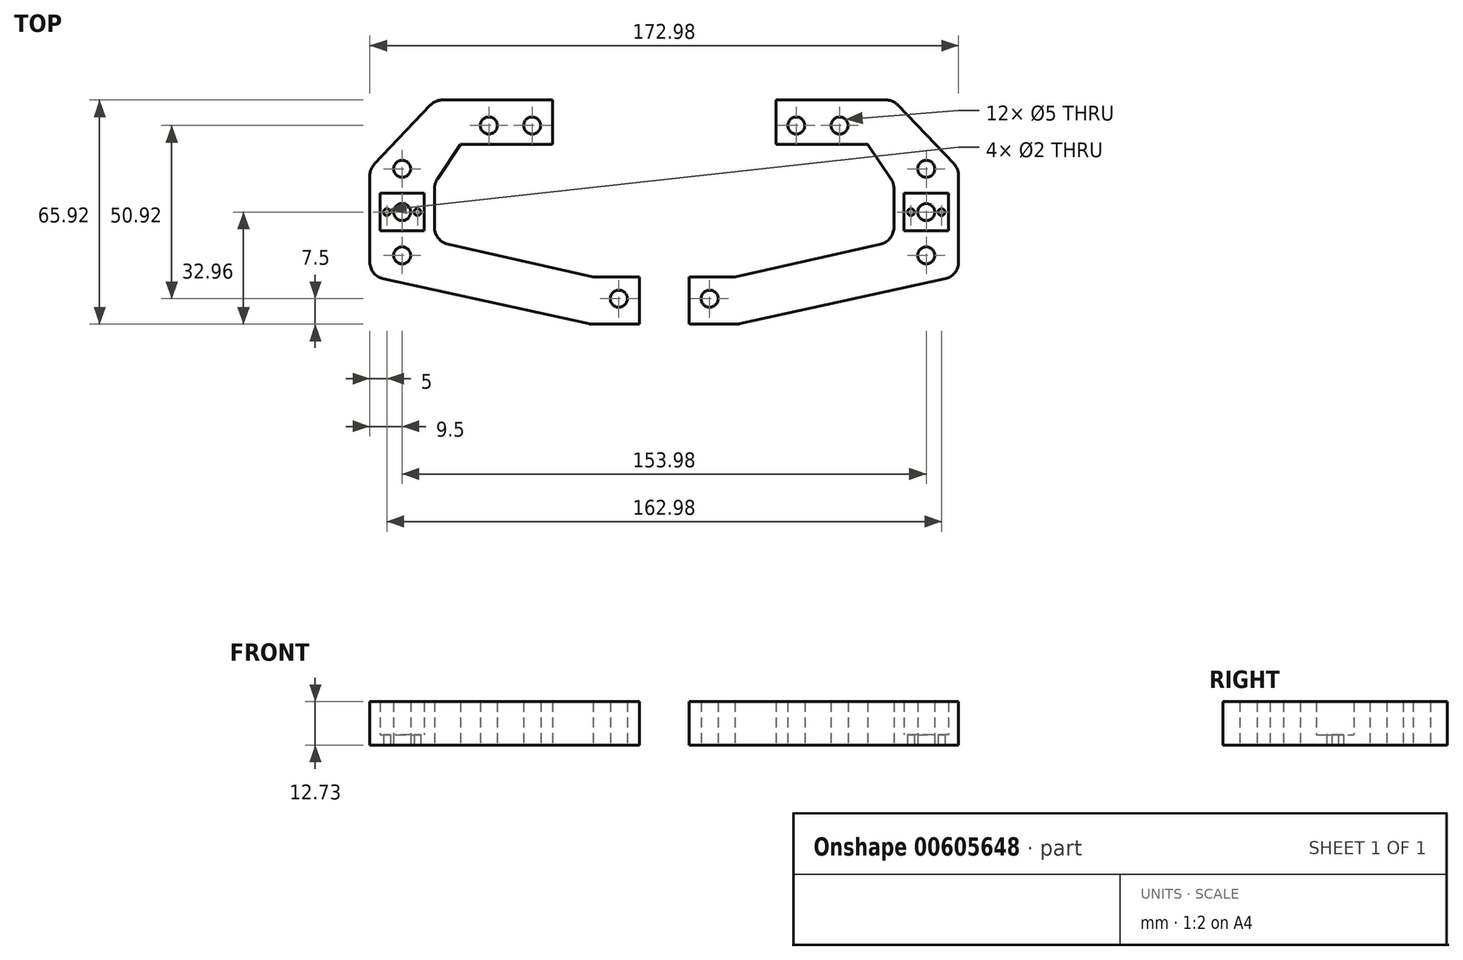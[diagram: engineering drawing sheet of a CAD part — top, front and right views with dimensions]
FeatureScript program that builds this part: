
annotation { "Feature Type Name" : "Feature", "Feature Type Description" : "" }
export const myFeature = defineFeature(function(context is Context, id is Id, definition is map)
    precondition{}
    {
        {
            var Q0;
            Q0=qCreatedBy(makeId("Top.planeOp"),FACE);
            var sketch = newSketch(context, id + "F0", { "sketchPlane" : qUnion([Q0])});
            skPoint(sketch, "E0", {"position": v(0, 0) * mm});
            skPoint(sketch, "E1", {"position": v(0, -50.92) * mm});
            skPoint(sketch, "E2", {"position": v(25.46, -50.92) * mm});
            skPoint(sketch, "E3", {"position": v(-12.73, 0) * mm});
            skPoint(sketch, "E4", {"position": v(0, -25.46) * mm});
            skPoint(sketch, "E5", {"position": v(-38.2, -25.46) * mm});
            skPoint(sketch, "E6.start.orphan", {"position": v(6, 0) * mm});
            skLineSegment(sketch, "E7", {"start": v(6, 5.5) * mm, "end": v(6, -5.5) * mm});
            skLineSegment(sketch, "E8", {"start": v(6, -5.5) * mm, "end": v(-21, -5.5) * mm});
            skLineSegment(sketch, "E9", {"start": v(31.46, -44.53) * mm, "end": v(17.95, -44.53) * mm});
            skCircle(sketch, "E10", {"center": v(-12.73, 0) * mm, "radius": 2.5 * mm});
            skCircle(sketch, "E11", {"center": v(0, 0) * mm, "radius": 2.5 * mm});
            skCircle(sketch, "E12", {"center": v(-38.2, -25.46) * mm, "radius": 2.5 * mm});
            skCircle(sketch, "E13", {"center": v(25.46, -50.92) * mm, "radius": 2.5 * mm});
            skPoint(sketch, "E14", {"position": v(6, 7.5) * mm});
            skLineSegment(sketch, "E15", {"start": v(6, 7.5) * mm, "end": v(6, 5.5) * mm});
            skLineSegment(sketch, "E16", {"start": v(17.2, -58.42) * mm, "end": v(31.46, -58.42) * mm});
            skPoint(sketch, "E17", {"position": v(31.46, -50.92) * mm});
            skLineSegment(sketch, "E18", {"start": v(31.46, -44.53) * mm, "end": v(31.46, -58.42) * mm});
            skPoint(sketch, "E19", {"position": v(31.46, -44.53) * mm});
            skPoint(sketch, "E20", {"position": v(31.46, -58.42) * mm});
            skLineSegment(sketch, "E21.bottom", {"start": v(-44.69, -30.96) * mm, "end": v(-31.69, -30.96) * mm});
            skLineSegment(sketch, "E21.top", {"start": v(-44.69, -19.96) * mm, "end": v(-31.69, -19.96) * mm});
            skLineSegment(sketch, "E21.left", {"start": v(-44.69, -30.96) * mm, "end": v(-44.69, -19.96) * mm});
            skLineSegment(sketch, "E21.right", {"start": v(-31.69, -30.96) * mm, "end": v(-31.69, -19.96) * mm});
            skPoint(sketch, "E22", {"position": v(-44.69, -25.46) * mm});
            skPoint(sketch, "E23", {"position": v(-31.69, -25.46) * mm});
            skPoint(sketch, "E24", {"position": v(-42.69, -25.46) * mm});
            skPoint(sketch, "E25", {"position": v(-33.69, -25.46) * mm});
            skCircle(sketch, "E26", {"center": v(-42.69, -25.46) * mm, "radius": 1 * mm});
            skCircle(sketch, "E27", {"center": v(-33.69, -25.46) * mm, "radius": 1 * mm});
            skLineSegment(sketch, "E28", {"start": v(-38.2, -25.46) * mm, "end": v(-38.2, -12.73) * mm});
            skLineSegment(sketch, "E29", {"start": v(-38.2, -25.46) * mm, "end": v(-38.2, -38.2) * mm});
            skLineSegment(sketch, "E30.0", {"start": v(-47.7, -33.96) * mm, "end": v(-47.7, -16.96) * mm});
            skLineSegment(sketch, "E30.1", {"start": v(-47.7, -33.96) * mm, "end": v(-28.69, -33.96) * mm});
            skLineSegment(sketch, "E30.2", {"start": v(-28.69, -33.96) * mm, "end": v(-28.69, -16.96) * mm});
            skLineSegment(sketch, "E30.3", {"start": v(-47.7, -16.96) * mm, "end": v(-28.69, -16.96) * mm});
            skLineSegment(sketch, "E31", {"start": v(-47.7, -16.96) * mm, "end": v(-47.7, -12.73) * mm});
            skLineSegment(sketch, "E32", {"start": v(-47.69, -12.73) * mm, "end": v(-28.42, 7.5) * mm});
            skCircle(sketch, "E33", {"center": v(-38.2, -12.73) * mm, "radius": 2.5 * mm});
            skCircle(sketch, "E34", {"center": v(-38.2, -38.2) * mm, "radius": 2.5 * mm});
            skLineSegment(sketch, "E35", {"start": v(17.19, -58.42) * mm, "end": v(-47.7, -44.2) * mm});
            skLineSegment(sketch, "E36", {"start": v(-47.7, -33.96) * mm, "end": v(-47.7, -44.2) * mm});
            skLineSegment(sketch, "E37", {"start": v(-21, -5.5) * mm, "end": v(-28.69, -16.96) * mm});
            skLineSegment(sketch, "E38", {"start": v(-28.7, -33.96) * mm, "end": v(17.95, -44.53) * mm});
            skLineSegment(sketch, "E39", {"start": v(6, 7.5) * mm, "end": v(-28.42, 7.5) * mm});
            skSolve(sketch);
        }
        {
            var Q0;
            Q0=makeQuery(id+"F0.imprint","IMPRINT",FACE,{"disambiguationData":[TD([[makeQuery(id+"F0.imprint","IMPRINT",EDGE,{"derivedFrom":sQuery(id+"F0.wireOp",EDGE,"fa019157-816a-4c44-b388-7206aec2f0b7.left")}),-1.0]])]});
            var Q1;
            Q1=makeQuery(id+"F0.imprint","IMPRINT",FACE,{"disambiguationData":[TD([[makeQuery(id+"F0.imprint","IMPRINT",EDGE,{"derivedFrom":sQuery(id+"F0.wireOp",EDGE,"E7")}),-1.0]])]});
            var Q2;
            {var subQ0=sQuery(id+"F0.wireOp",EDGE,"bcnTlRam-B4tb-dVcL-KTe7-YnhKrGYre8tU");Q2=makeQuery(id+"F0.imprint","IMPRINT",FACE,{"disambiguationData":[TD([[makeQuery(id+"F0.imprint","IMPRINT",EDGE,{"derivedFrom":subQ0}),-1.0]])]});}
            var Q3;
            Q3=makeQuery(id+"F0.imprint","IMPRINT",FACE,{"disambiguationData":[TD([[makeQuery(id+"F0.imprint","IMPRINT",EDGE,{"derivedFrom":sQuery(id+"F0.wireOp",EDGE,"E9")}),1.0]])]});
            var Q4;
            {var subQ5=sQuery(id+"F0.wireOp",EDGE,"E21.right");Q4=makeQuery(id+"F0.imprint","IMPRINT",FACE,{"disambiguationData":[TD([[makeQuery(id+"F0.imprint","IMPRINT",EDGE,{"derivedFrom":subQ5}),-1.0]])]});}
            var Q5;
            {var subQ0=sQuery(id+"F0.wireOp",EDGE,"E21.left");Q5=makeQuery(id+"F0.imprint","IMPRINT",FACE,{"disambiguationData":[TD([[makeQuery(id+"F0.imprint","IMPRINT",EDGE,{"derivedFrom":subQ0}),1.0]])]});}
            extrude(context, id + "F1", {"entities" : qUnion([Q0, Q1, Q2, Q3, Q4, Q5]), "depth" : 12.73 * mm, "offsetDistance" : 25 * mm});
        }
        {
            var Q0;
            Q0=makeQuery(id+"F0.imprint","IMPRINT",FACE,{"disambiguationData":[TD([[makeQuery(id+"F0.imprint","IMPRINT",EDGE,{"derivedFrom":sQuery(id+"F0.wireOp",EDGE,"E12")}),-1.0]])]});
            extrude(context, id + "F2", {"entities" : qUnion([Q0]), "operationType" : NewBodyOperationType.ADD, "depth" : 3 * mm, "offsetDistance" : 25 * mm});
        }
        {
            var Q0;
            Q0=makeQuery(id+"F1.opExtrude","SWEPT_EDGE",EDGE,{"disambiguationData":[OSD([sQuery(id+"F0.wireOp",EDGE,"E32"),sQuery(id+"F0.wireOp",EDGE,"E39")])]});
            var Q1;
            Q1=makeQuery(id+"F1.opExtrude","SWEPT_EDGE",EDGE,{"disambiguationData":[OSD([sQuery(id+"F0.wireOp",EDGE,"E31"),sQuery(id+"F0.wireOp",EDGE,"E32")])]});
            var Q2;
            Q2=makeQuery(id+"F1.opExtrude","SWEPT_EDGE",EDGE,{"disambiguationData":[OSD([sQuery(id+"F0.wireOp",EDGE,"E35"),sQuery(id+"F0.wireOp",EDGE,"E36")])]});
            var Q3;
            Q3=makeQuery(id+"F1.opExtrude","SWEPT_EDGE",EDGE,{"disambiguationData":[OSD([sQuery(id+"F0.wireOp",EDGE,"E16"),sQuery(id+"F0.wireOp",EDGE,"E35")])]});
            fillet(context, id + "F3", {"entities" : qUnion([Q0, Q1, Q2, Q3]), "radius" : 5 * mm, "tangentPropagation" : true, "allowEdgeOverflow" : false});
        }
        {
            var Q0;
            Q0=makeQuery(id+"F1.opExtrude","SWEPT_EDGE",EDGE,{"disambiguationData":[OSD([sQuery(id+"F0.wireOp",EDGE,"E30.2"),sQuery(id+"F0.wireOp",EDGE,"E30.3"),sQuery(id+"F0.wireOp",EDGE,"E37")])]});
            var Q1;
            Q1=makeQuery(id+"F1.opExtrude","SWEPT_EDGE",EDGE,{"disambiguationData":[OSD([sQuery(id+"F0.wireOp",EDGE,"E30.1"),sQuery(id+"F0.wireOp",EDGE,"E30.2"),sQuery(id+"F0.wireOp",EDGE,"E38")])]});
            fillet(context, id + "F4", {"entities" : qUnion([Q0, Q1]), "radius" : 5 * mm, "tangentPropagation" : true, "allowEdgeOverflow" : false});
        }
        {
            var Q0;
            Q0=makeQuery(id+"F1.opExtrude","SWEPT_BODY",BODY,{"disambiguationData":[OSD([sQuery(id+"F0.wireOp",EDGE,"E7"),sQuery(id+"F0.wireOp",EDGE,"E8"),sQuery(id+"F0.wireOp",EDGE,"E9"),sQuery(id+"F0.wireOp",EDGE,"bcnTlRam-B4tb-dVcL-KTe7-YnhKrGYre8tU"),sQuery(id+"F0.wireOp",EDGE,"wtGR8LKO-41am-TRb3-HE83-JQrdiI2E5iHG"),sQuery(id+"F0.wireOp",EDGE,"E10"),sQuery(id+"F0.wireOp",EDGE,"E11"),sQuery(id+"F0.wireOp",EDGE,"E13"),sQuery(id+"F0.wireOp",EDGE,"rJLetVZT-IXvu-TdCA-2Rpv-SM2PC27GVaC4"),sQuery(id+"F0.wireOp",EDGE,"eD1ADjsr-uSCu-Brk3-ThtO-dkbjbpZPNoQs"),sQuery(id+"F0.wireOp",EDGE,"E15"),sQuery(id+"F0.wireOp",EDGE,"2IS2hVsA-Xzl8-U664-KEqC-C2BQuWRoZGjc"),sQuery(id+"F0.wireOp",EDGE,"E16"),sQuery(id+"F0.wireOp",EDGE,"E18"),sQuery(id+"F0.wireOp",EDGE,"E21.bottom"),sQuery(id+"F0.wireOp",EDGE,"E21.top"),sQuery(id+"F0.wireOp",EDGE,"E21.left"),sQuery(id+"F0.wireOp",EDGE,"E21.right"),sQuery(id+"F0.wireOp",EDGE,"FevVS2ti-XUGI-zkMm-Zb2I-lsAMRADx3wao"),sQuery(id+"F0.wireOp",EDGE,"z31AdJfX-5Frq-LdcY-bJIX-4YXTuY3hfW2P"),sQuery(id+"F0.wireOp",EDGE,"a1cfb847-266f-4aee-b1e6-413f9c7dd414.0"),sQuery(id+"F0.wireOp",EDGE,"2vp7eMst-deK1-u27D-Jkh1-uvNu9UCNG65P"),sQuery(id+"F0.wireOp",EDGE,"3uUYc8cM-QZgS-e0Kj-1ilK-pYgc2PbXZ3LF"),sQuery(id+"F0.wireOp",EDGE,"a9fa6418-34e3-4f35-bcd8-d294bacf0691.0"),sQuery(id+"F0.wireOp",EDGE,"oyA7nse3-oMkV-IIfA-EYwd-oT6ugLlugK1s"),sQuery(id+"F0.wireOp",EDGE,"44JFaFFQ-S6n4-xKe0-8Ien-k9RlxjsEQfp2"),sQuery(id+"F0.wireOp",EDGE,"kwwnNI9h-u1H1-rU73-2PpV-EkyO41qdpQwr")])]});
            transform(context, id + "F5", {"entities" : qUnion([Q0]), "transformType" : TransformType.TRANSLATION_3D, "dx" : -38.8 * mm, "dy" : 0 * mm, "dz" : 0 * mm, "makeCopy" : false});
        }
        {
            var Q0;
            Q0=makeQuery(id+"F1.opExtrude","SWEPT_BODY",BODY,{"disambiguationData":[OSD([sQuery(id+"F0.wireOp",EDGE,"E7"),sQuery(id+"F0.wireOp",EDGE,"E8"),sQuery(id+"F0.wireOp",EDGE,"E9"),sQuery(id+"F0.wireOp",EDGE,"bcnTlRam-B4tb-dVcL-KTe7-YnhKrGYre8tU"),sQuery(id+"F0.wireOp",EDGE,"wtGR8LKO-41am-TRb3-HE83-JQrdiI2E5iHG"),sQuery(id+"F0.wireOp",EDGE,"E10"),sQuery(id+"F0.wireOp",EDGE,"E11"),sQuery(id+"F0.wireOp",EDGE,"E13"),sQuery(id+"F0.wireOp",EDGE,"rJLetVZT-IXvu-TdCA-2Rpv-SM2PC27GVaC4"),sQuery(id+"F0.wireOp",EDGE,"eD1ADjsr-uSCu-Brk3-ThtO-dkbjbpZPNoQs"),sQuery(id+"F0.wireOp",EDGE,"E15"),sQuery(id+"F0.wireOp",EDGE,"2IS2hVsA-Xzl8-U664-KEqC-C2BQuWRoZGjc"),sQuery(id+"F0.wireOp",EDGE,"E16"),sQuery(id+"F0.wireOp",EDGE,"E18"),sQuery(id+"F0.wireOp",EDGE,"E21.bottom"),sQuery(id+"F0.wireOp",EDGE,"E21.top"),sQuery(id+"F0.wireOp",EDGE,"E21.left"),sQuery(id+"F0.wireOp",EDGE,"E21.right"),sQuery(id+"F0.wireOp",EDGE,"FevVS2ti-XUGI-zkMm-Zb2I-lsAMRADx3wao"),sQuery(id+"F0.wireOp",EDGE,"z31AdJfX-5Frq-LdcY-bJIX-4YXTuY3hfW2P"),sQuery(id+"F0.wireOp",EDGE,"a1cfb847-266f-4aee-b1e6-413f9c7dd414.0"),sQuery(id+"F0.wireOp",EDGE,"2vp7eMst-deK1-u27D-Jkh1-uvNu9UCNG65P"),sQuery(id+"F0.wireOp",EDGE,"3uUYc8cM-QZgS-e0Kj-1ilK-pYgc2PbXZ3LF"),sQuery(id+"F0.wireOp",EDGE,"a9fa6418-34e3-4f35-bcd8-d294bacf0691.0"),sQuery(id+"F0.wireOp",EDGE,"oyA7nse3-oMkV-IIfA-EYwd-oT6ugLlugK1s"),sQuery(id+"F0.wireOp",EDGE,"44JFaFFQ-S6n4-xKe0-8Ien-k9RlxjsEQfp2"),sQuery(id+"F0.wireOp",EDGE,"kwwnNI9h-u1H1-rU73-2PpV-EkyO41qdpQwr")])]});
            var Q1;
            Q1=qCreatedBy(makeId("Right.planeOp"),FACE);
            mirror(context, id + "F6", {"entities" : qUnion([Q0]), "mirrorPlane" : qUnion([Q1])});
        }
    });
